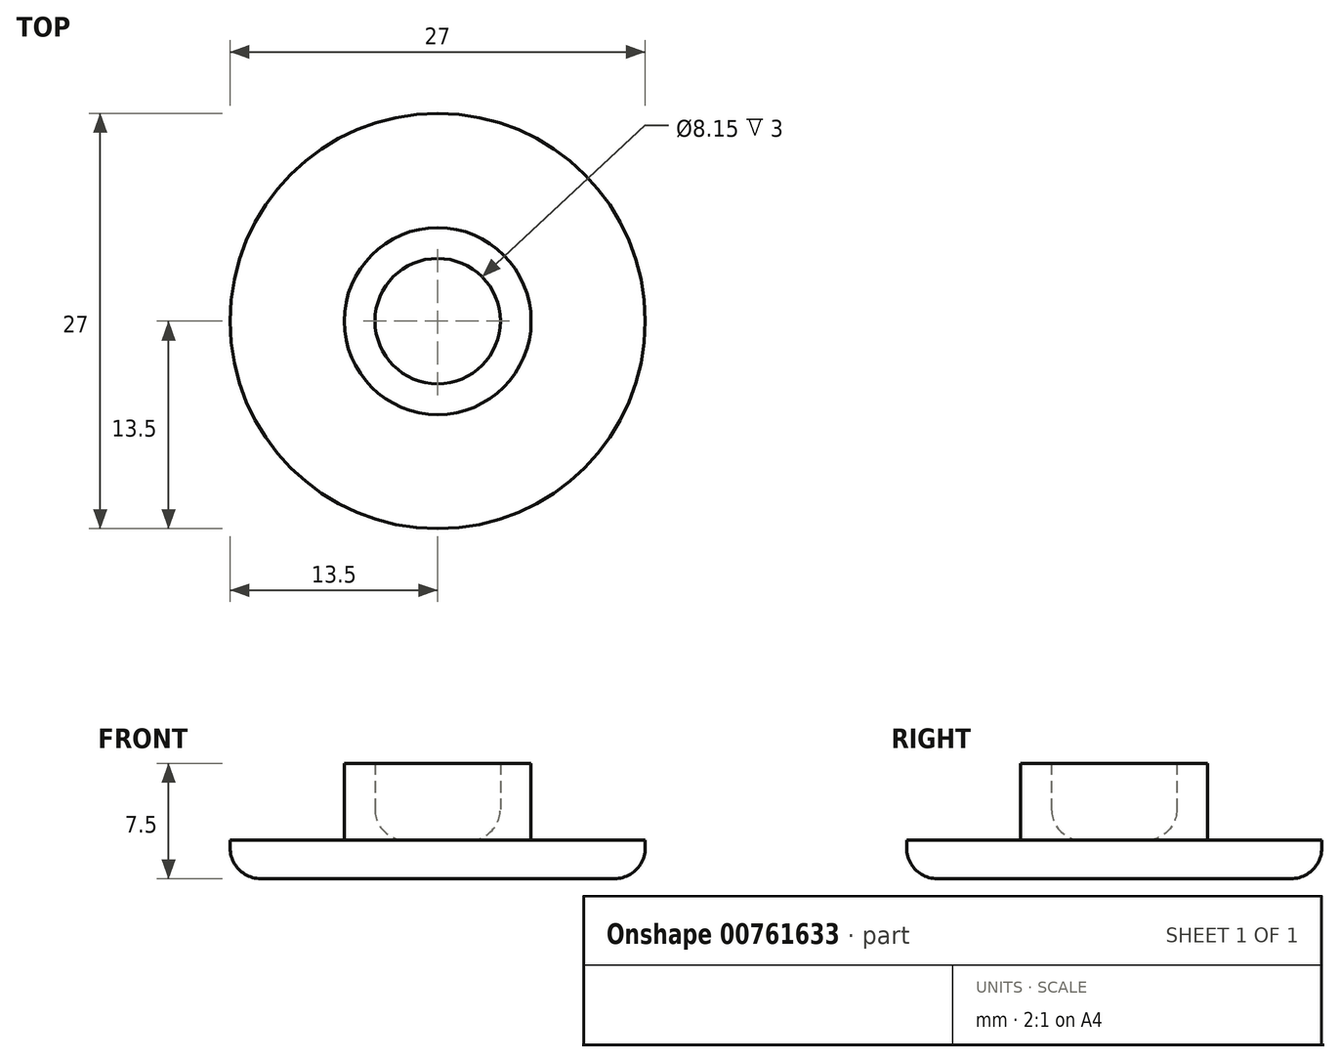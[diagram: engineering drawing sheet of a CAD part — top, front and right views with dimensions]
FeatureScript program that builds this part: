
annotation { "Feature Type Name" : "Feature", "Feature Type Description" : "" }
export const myFeature = defineFeature(function(context is Context, id is Id, definition is map)
    precondition{}
    {
        {
            var Q0;
            Q0=qCreatedBy(makeId("Top.planeOp"),FACE);
            var sketch = newSketch(context, id + "F0", { "sketchPlane" : qUnion([Q0])});
            skCircle(sketch, "E0", {"center": v(0, 0) * mm, "radius": 13.5 * mm});
            skSolve(sketch);
        }
        {
            var Q0;
            Q0 = qSketchRegion(id + "F0", true);
            extrude(context, id + "F1", {"entities" : qUnion([Q0]), "depth" : 2.5 * mm, "offsetDistance" : 25 * mm});
        }
        {
            var Q0;
            Q0=makeQuery(id+"F1.opExtrude","CAP_FACE",FACE,{"disambiguationData":[OSD([sQuery(id+"F0.wireOp",EDGE,"E0")])],"isStart":false});
            var sketch = newSketch(context, id + "F2", { "sketchPlane" : qUnion([Q0])});
            skCircle(sketch, "E1", {"center": v(0, 0) * mm, "radius": 6.08 * mm});
            skCircle(sketch, "E2", {"center": v(0, 0) * mm, "radius": 4.08 * mm});
            skSolve(sketch);
        }
        {
            var Q0;
            Q0=makeQuery(id+"F2.imprint","IMPRINT",FACE,{"disambiguationData":[TD([[makeQuery(id+"F2.imprint","IMPRINT",EDGE,{"derivedFrom":sQuery(id+"F2.wireOp",EDGE,"E1")}),1.0]])]});
            extrude(context, id + "F3", {"entities" : qUnion([Q0]), "operationType" : NewBodyOperationType.ADD, "depth" : 5 * mm, "offsetDistance" : 25 * mm});
        }
        {
            var Q0;
            Q0=makeQuery(id+"F3.opExtrude","CAP_EDGE",EDGE,{"disambiguationData":[OSD([sQuery(id+"F2.wireOp",EDGE,"E2")])],"isStart":true});
            fillet(context, id + "F4", {"entities" : qUnion([Q0]), "radius" : 2 * mm, "tangentPropagation" : true, "allowEdgeOverflow" : false});
        }
        {
            var Q0;
            Q0=makeQuery(id+"F1.opExtrude","CAP_EDGE",EDGE,{"disambiguationData":[OSD([sQuery(id+"F0.wireOp",EDGE,"E0")])],"isStart":true});
            fillet(context, id + "F5", {"entities" : qUnion([Q0]), "radius" : 2 * mm, "tangentPropagation" : true, "allowEdgeOverflow" : false});
        }
    });
